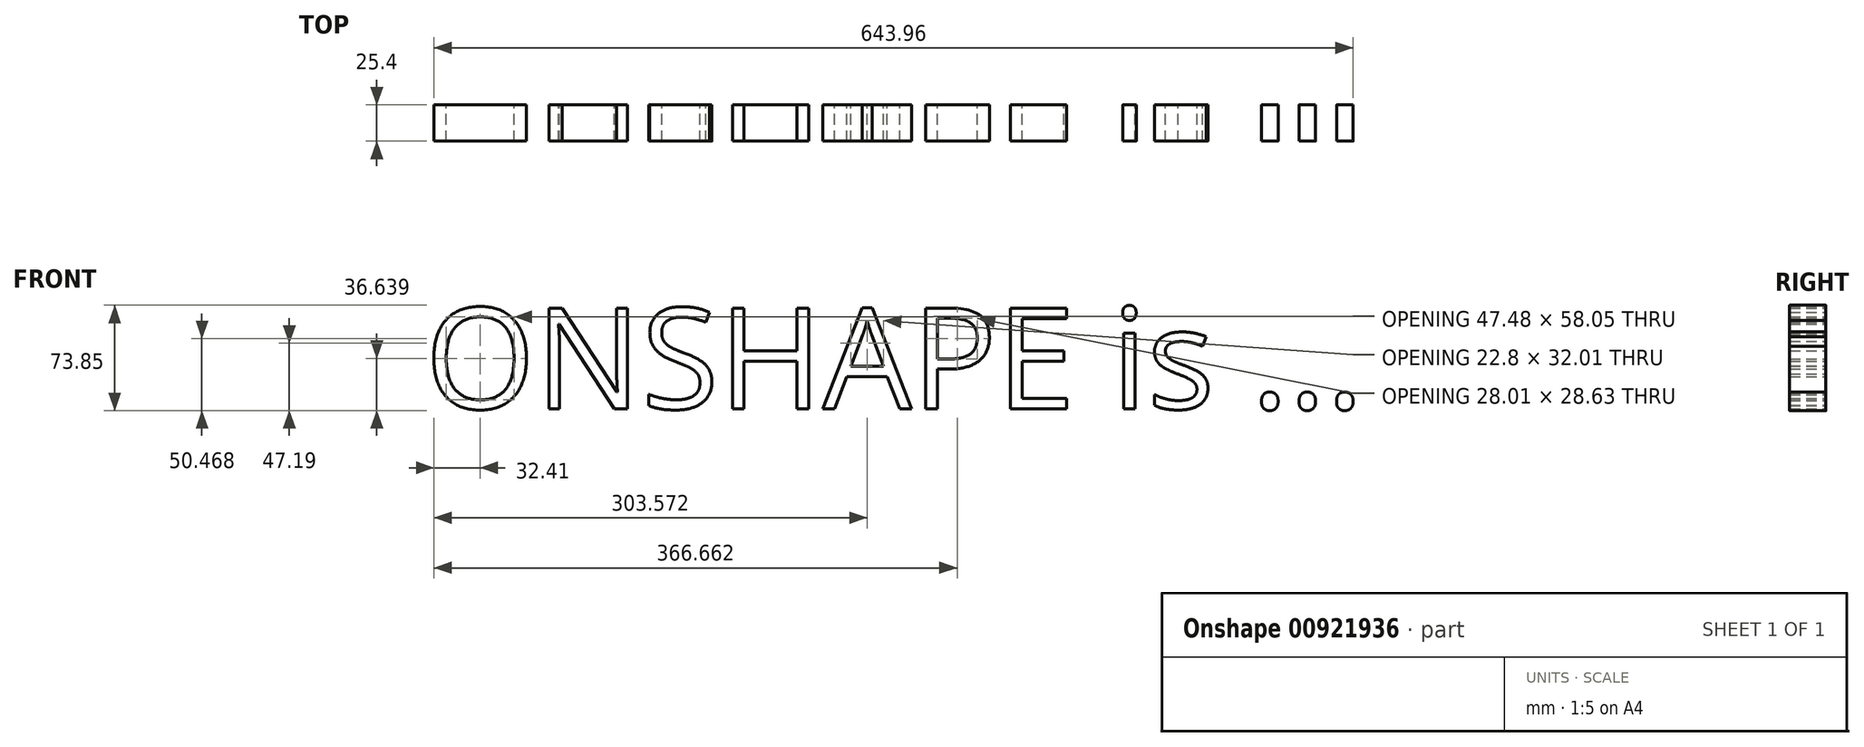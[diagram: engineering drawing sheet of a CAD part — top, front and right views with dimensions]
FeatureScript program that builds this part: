
annotation { "Feature Type Name" : "Feature", "Feature Type Description" : "" }
export const myFeature = defineFeature(function(context is Context, id is Id, definition is map)
    precondition{}
    {
        {
            var Q0;
            Q0=qCreatedBy(makeId("Front.planeOp"),FACE);
            var sketch = newSketch(context, id + "F0", { "sketchPlane" : qUnion([Q0])});
            skText(sketch, "E0", { "text": "ONSHAPE is ...", "fontName": "OpenSans-Regular.ttf"});
            const initialGuessF0  = {"E0": [-0.11445, -0.03275, 1, 0, 0.07108]};
            skSetInitialGuess(sketch, initialGuessF0);
            skSolve(sketch);
        }
        {
            var Q0;
            Q0 = qSketchRegion(id + "F0", true);
            extrude(context, id + "F1", {"entities" : qUnion([Q0]), "depth" : 25.4 * mm, "offsetDistance" : 25.4 * mm});
        }
    });
